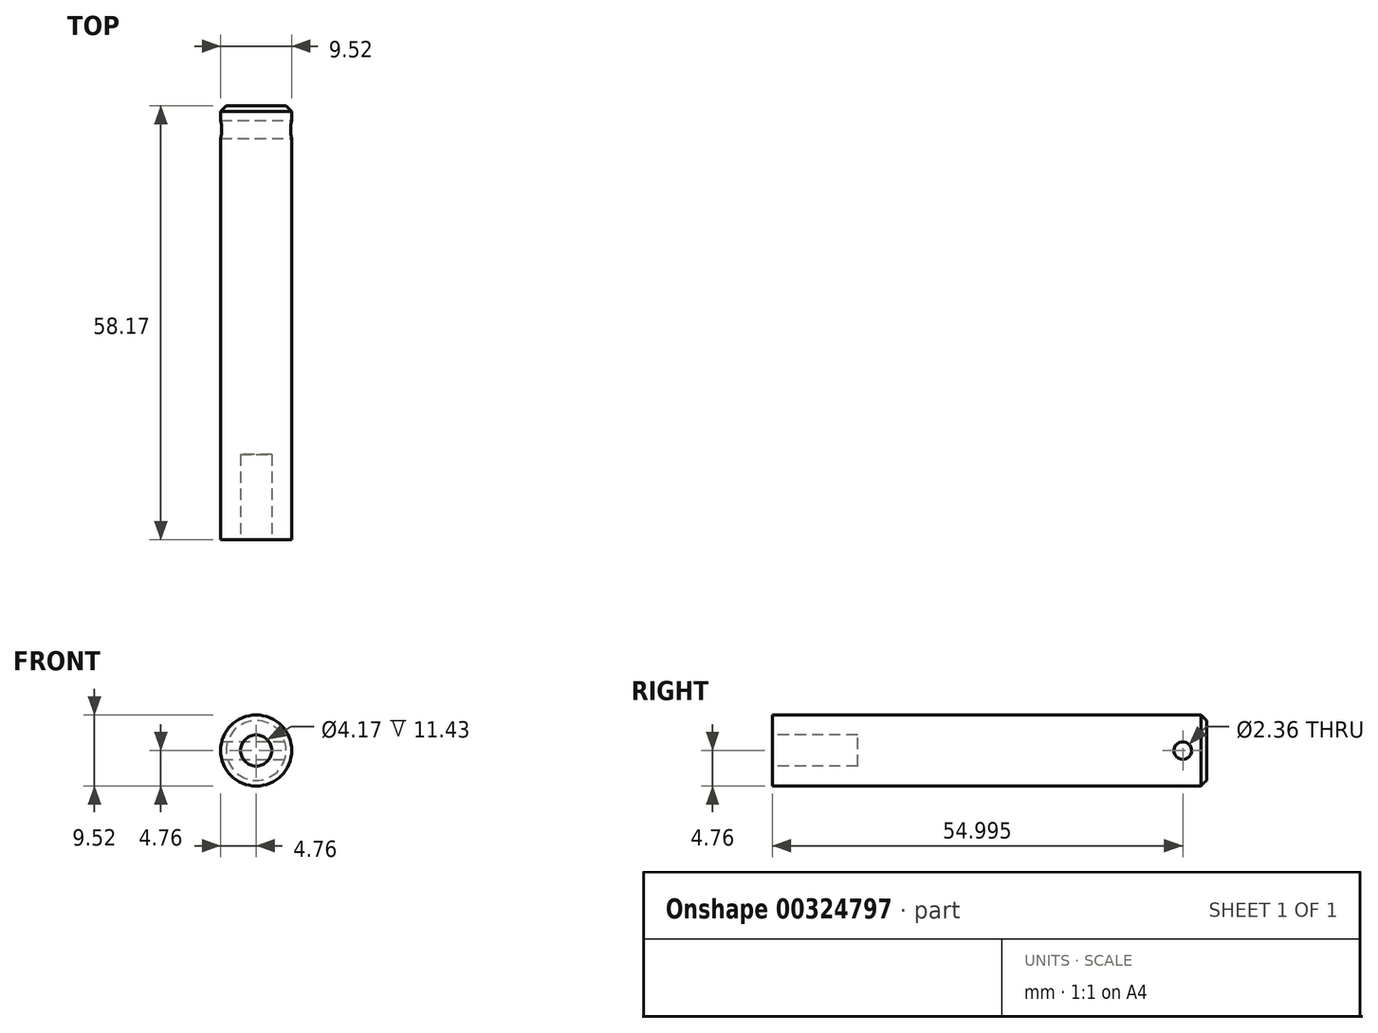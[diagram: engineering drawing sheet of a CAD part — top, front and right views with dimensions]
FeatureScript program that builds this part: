
annotation { "Feature Type Name" : "Feature", "Feature Type Description" : "" }
export const myFeature = defineFeature(function(context is Context, id is Id, definition is map)
    precondition{}
    {
        {
            var Q0;
            Q0=qCreatedBy(makeId("Front.planeOp"),FACE);
            var sketch = newSketch(context, id + "F0", { "sketchPlane" : qUnion([Q0])});
            skCircle(sketch, "E0", {"center": v(0, 0) * mm, "radius": 4.76 * mm});
            skSolve(sketch);
        }
        {
            var Q0;
            Q0=makeQuery(id+"F0.imprint","IMPRINT",FACE,{"disambiguationData":[TD([[makeQuery(id+"F0.imprint","IMPRINT",EDGE,{"derivedFrom":sQuery(id+"F0.wireOp",EDGE,"E0")}),1.0]])]});
            extrude(context, id + "F1", {"entities" : qUnion([Q0]), "depth" : 58.17 * mm, "offsetDistance" : 25.4 * mm});
        }
        {
            var Q0;
            Q0=makeQuery(id+"F1.opExtrude","CAP_FACE",FACE,{"disambiguationData":[OSD([sQuery(id+"F0.wireOp",EDGE,"E0")])],"isStart":false});
            var sketch = newSketch(context, id + "F2", { "sketchPlane" : qUnion([Q0])});
            skCircle(sketch, "E1", {"center": v(0, 0) * mm, "radius": 2.08 * mm});
            skSolve(sketch);
        }
        {
            var Q0;
            Q0=makeQuery(id+"F2.imprint","IMPRINT",FACE,{"disambiguationData":[TD([[makeQuery(id+"F2.imprint","IMPRINT",EDGE,{"derivedFrom":sQuery(id+"F2.wireOp",EDGE,"E1")}),1.0]])]});
            extrude(context, id + "F3", {"entities" : qUnion([Q0]), "operationType" : NewBodyOperationType.REMOVE, "oppositeDirection" : true, "depth" : 11.43 * mm, "offsetDistance" : 25.4 * mm});
        }
        {
            var Q0;
            Q0=qCreatedBy(makeId("Right.planeOp"),FACE);
            cPlane(context, id + "F4", {"entities" : qUnion([Q0]), "cplaneType" : CPlaneType.OFFSET, "offset" : 4.8 * mm, "width" : 152.4 * mm, "height" : 152.4 * mm});
        }
        {
            var Q0;
            Q0=qCreatedBy(id+"F4.planeOp",FACE);
            var sketch = newSketch(context, id + "F5", { "sketchPlane" : qUnion([Q0])});
            skCircle(sketch, "E2", {"center": v(-3.18, 0) * mm, "radius": 1.18 * mm});
            skSolve(sketch);
        }
        {
            var Q0;
            Q0=makeQuery(id+"F5.imprint","IMPRINT",FACE,{"disambiguationData":[TD([[makeQuery(id+"F5.imprint","IMPRINT",EDGE,{"derivedFrom":sQuery(id+"F5.wireOp",EDGE,"E2")}),1.0]])]});
            extrude(context, id + "F6", {"entities" : qUnion([Q0]), "operationType" : NewBodyOperationType.REMOVE, "oppositeDirection" : true, "depth" : 10.16 * mm, "offsetDistance" : 25.4 * mm});
        }
        {
            var Q0;
            Q0=makeQuery(id+"F1.opExtrude","CAP_EDGE",EDGE,{"disambiguationData":[OSD([sQuery(id+"F0.wireOp",EDGE,"E0")])],"isStart":true});
            chamfer(context, id + "F7", {"entities" : qUnion([Q0]), "width" : 0.76 * mm, "tangentPropagation" : true});
        }
    });
